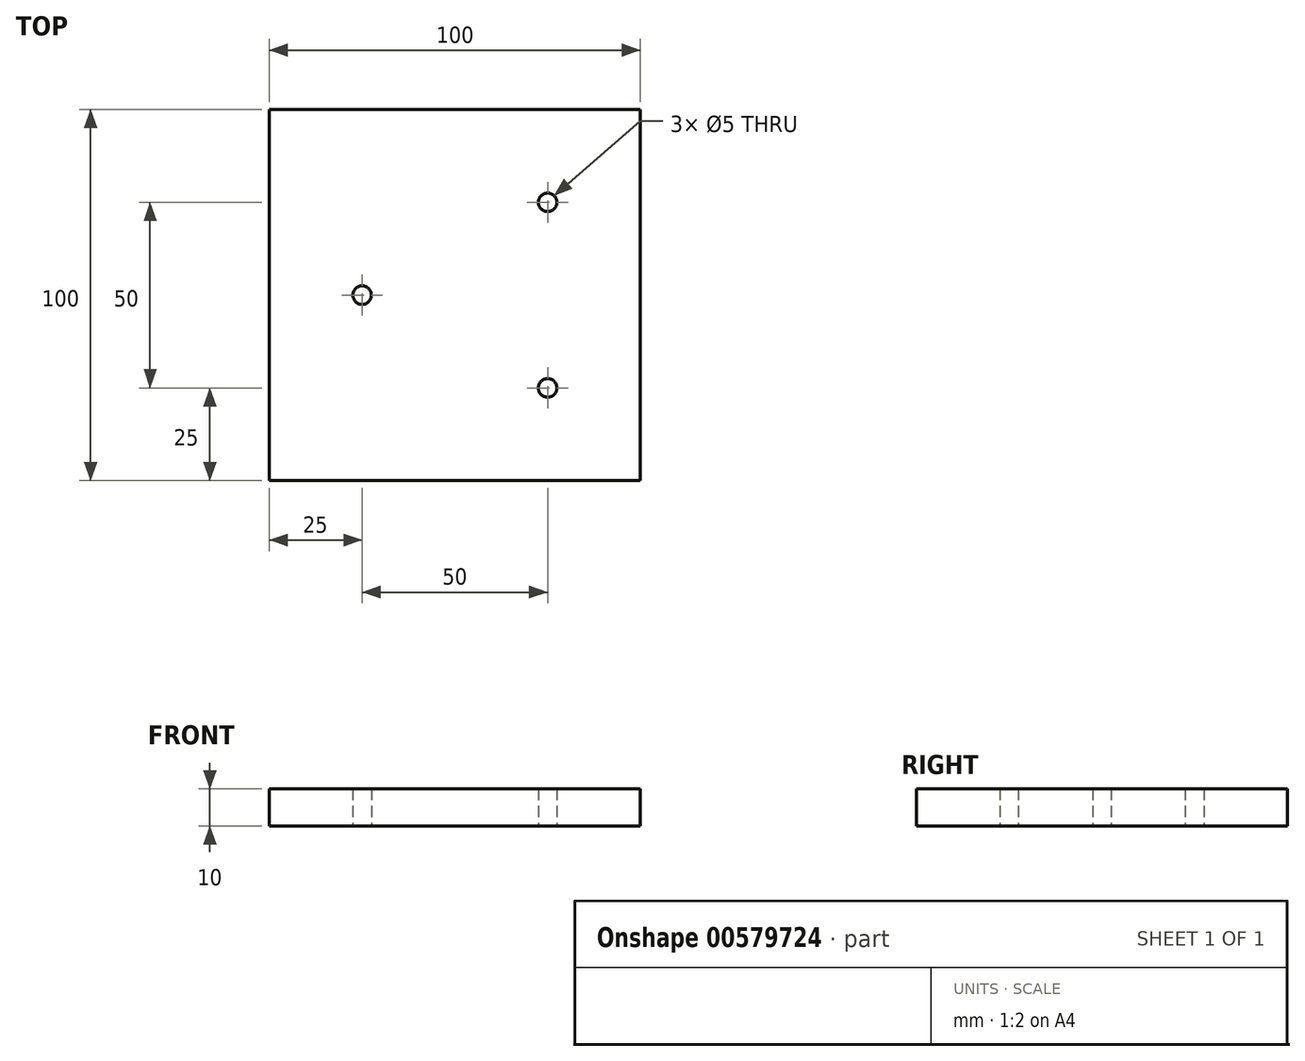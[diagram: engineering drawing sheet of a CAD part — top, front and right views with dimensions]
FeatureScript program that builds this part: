
annotation { "Feature Type Name" : "Feature", "Feature Type Description" : "" }
export const myFeature = defineFeature(function(context is Context, id is Id, definition is map)
    precondition{}
    {
        {
            var Q0;
            Q0=qCreatedBy(makeId("Top.planeOp"),FACE);
            var sketch = newSketch(context, id + "F0", { "sketchPlane" : qUnion([Q0])});
            skLineSegment(sketch, "E0.bottom", {"start": v(0, 0) * mm, "end": v(100, 0) * mm});
            skLineSegment(sketch, "E0.top", {"start": v(0, 100) * mm, "end": v(100, 100) * mm});
            skLineSegment(sketch, "E0.left", {"start": v(0, 0) * mm, "end": v(0, 100) * mm});
            skLineSegment(sketch, "E0.right", {"start": v(100, 0) * mm, "end": v(100, 100) * mm});
            skPoint(sketch, "E1", {"position": v(75, 75) * mm});
            skPoint(sketch, "E2", {"position": v(75, 25) * mm});
            skPoint(sketch, "E3", {"position": v(25, 50) * mm});
            skSolve(sketch);
        }
        {
            var Q0;
            Q0=makeQuery(id+"F0.imprint","IMPRINT",FACE,{"disambiguationData":[TD([[makeQuery(id+"F0.imprint","IMPRINT",EDGE,{"derivedFrom":sQuery(id+"F0.wireOp",EDGE,"E0.bottom")}),1.0]])]});
            extrude(context, id + "F1", {"entities" : qUnion([Q0]), "depth" : 10 * mm, "offsetDistance" : 25 * mm});
        }
        {
            var Q0;
            Q0=sQuery(id+"F0.wireOp",VERTEX,"E1");
            var Q1;
            Q1=sQuery(id+"F0.wireOp",VERTEX,"E2");
            var Q2;
            Q2=sQuery(id+"F0.wireOp",VERTEX,"E3");
            var Q3;
            Q3=makeQuery(id+"F1.opExtrude","SWEPT_BODY",BODY,{"disambiguationData":[OSD([sQuery(id+"F0.wireOp",EDGE,"E0.bottom"),sQuery(id+"F0.wireOp",EDGE,"E0.top"),sQuery(id+"F0.wireOp",EDGE,"E0.left"),sQuery(id+"F0.wireOp",EDGE,"E0.right")])]});
            hole(context, id + "F2", {"style" : HoleStyle.SIMPLE, "endStyle" : HoleEndStyle.THROUGH, "oppositeDirection" : true, "standardTappedOrClearance" : lookupTablePath({ "standard" : "ISO", "engagement" : "75%", "pitch" : "1 mm", "size" : "M6", "type" : "Tapped" }), "standardBlindInLast" : lookupTablePath({ "standard" : "ISO", "engagement" : "75%", "pitch" : "1 mm", "size" : "M6", "type" : "Tapped" }), "holeDiameter" : 5 * mm, "showTappedDepth" : true, "isTappedThrough" : true, "tappedDepth" : 12 * mm, "tapClearance" : 3, "startFromSketch" : true, "locations" : qUnion([Q0, Q1, Q2]), "scope" : qUnion([Q3]), "majorDiameter" : 6 * mm});
        }
    });
